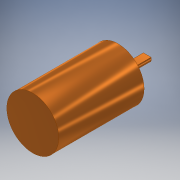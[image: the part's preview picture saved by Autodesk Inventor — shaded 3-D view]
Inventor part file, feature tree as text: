
AUTODESK INVENTOR PART (.ipt)
format: ipt  version: 2018 (Build 220112000, 112)  size: 119,808 bytes
history: native  units: mm
features: extrude x4, sketch x4
ambient origin geometry x8: Origin, YZ Plane, XZ Plane, XY Plane, X Axis, Y Axis, Z Axis, Center Point
bodies: 实体1 (feature_tree)
feature tree (8):
  extrude  "拉伸1"  Depth=41.0mm TaperAngle=0.0deg
  extrude  "拉伸2"  Depth=3.0mm TaperAngle=0.0deg
  sketch  "草图3"  dims[d6=4.0mm d7=11.0mm d8=0.0mm]
  extrude  "拉伸3"  Depth=11.0mm TaperAngle=0.0deg
  extrude  "拉伸4"  Depth=2.0mm
  sketch  "草图1"  dims[d0=25.0mm d1=41.0mm d2=0.0mm]
  sketch  "草图2"  dims[d3=7.0mm d4=3.0mm d5=0.0mm]
  sketch  "草图4"  dims[d9=0.8mm d10=2.0mm d11=11.0mm d12=0.0mm]
